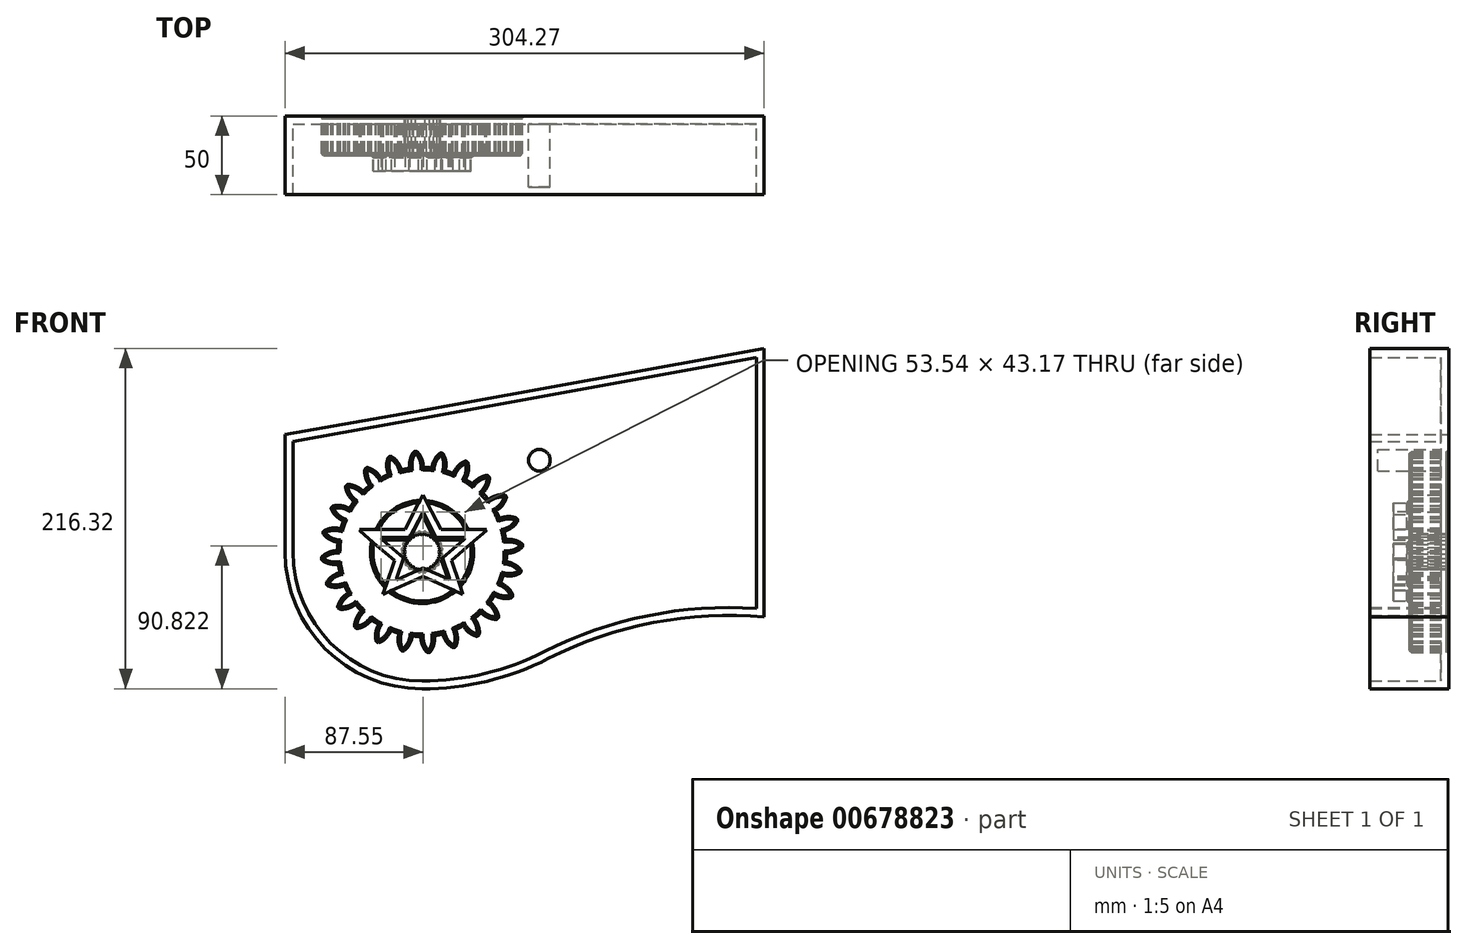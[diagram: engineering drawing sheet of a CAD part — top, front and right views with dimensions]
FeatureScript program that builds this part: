
annotation { "Feature Type Name" : "Feature", "Feature Type Description" : "" }
export const myFeature = defineFeature(function(context is Context, id is Id, definition is map)
    precondition{}
    {
        {
            var Q0;
            Q0=qCreatedBy(makeId("Front.planeOp"),FACE);
            var sketch = newSketch(context, id + "F0", { "sketchPlane" : qUnion([Q0])});
            skCircle(sketch, "E0", {"center": v(0, 0) * mm, "radius": 53.72 * mm});
            skCircle(sketch, "E1", {"center": v(0, 0) * mm, "radius": 58.67 * mm, "construction": true});
            skCircle(sketch, "E2", {"center": v(0, 0) * mm, "radius": 63.5 * mm, "construction": true});
            skLineSegment(sketch, "E3", {"start": v(0, 0) * mm, "end": v(0, 90.28) * mm, "construction": true});
            skLineSegment(sketch, "E4", {"start": v(0, 0) * mm, "end": v(-5.89, 89.83) * mm, "construction": true});
            skLineSegment(sketch, "E5", {"start": v(0, 58.67) * mm, "end": v(-86.47, 27.2) * mm, "construction": true});
            skLineSegment(sketch, "E6", {"start": v(0, 58.67) * mm, "end": v(-89.07, 58.67) * mm, "construction": true});
            skCircle(sketch, "E7", {"center": v(0, 0) * mm, "radius": 55.14 * mm, "construction": true});
            skCircle(sketch, "E8", {"center": v(0, 58.67) * mm, "radius": 14.6 * mm, "construction": true});
            skCircle(sketch, "E9", {"center": v(-13.72, 53.68) * mm, "radius": 14.6 * mm, "construction": true});
            skArc(sketch, "E10", {"start": v(0, 58.67) * mm, "mid": v(-1.18, 61.2) * mm, "end": v(-2.86, 63.44) * mm});
            skArc(sketch, "E11", {"start": v(0.88, 53.71) * mm, "mid": v(0.64, 56.23) * mm, "end": v(0, 58.67) * mm});
            skArc(sketch, "E12.MirrorCS", {"start": v(-7.88, 53.14) * mm, "mid": v(-7.97, 55.66) * mm, "end": v(-7.66, 58.17) * mm});
            skArc(sketch, "E13.MirrorCS", {"start": v(-7.66, 58.17) * mm, "mid": v(-6.82, 60.83) * mm, "end": v(-5.45, 63.27) * mm});
            skArc(sketch, "E14", {"start": v(-2.86, 63.44) * mm, "mid": v(-4.2, 63.93) * mm, "end": v(-5.45, 63.27) * mm});
            skCircle(sketch, "E15", {"center": v(0, 0) * mm, "radius": 31.25 * mm});
            skLineSegment(sketch, "E16", {"start": v(0, 23.83) * mm, "end": v(8.38, 7.72) * mm});
            skLineSegment(sketch, "E17", {"start": v(8.38, 7.72) * mm, "end": v(26.77, 7.72) * mm});
            skLineSegment(sketch, "E18", {"start": v(26.77, 7.72) * mm, "end": v(12.19, -4.72) * mm});
            skLineSegment(sketch, "E19", {"start": v(12.19, -4.72) * mm, "end": v(16.83, -18.55) * mm});
            skLineSegment(sketch, "E20", {"start": v(16.83, -18.55) * mm, "end": v(0, -10.88) * mm});
            skLineSegment(sketch, "E21.MirrorCS", {"start": v(0, 23.83) * mm, "end": v(-8.38, 7.72) * mm});
            skLineSegment(sketch, "E22.MirrorCS", {"start": v(-8.38, 7.72) * mm, "end": v(-26.77, 7.72) * mm});
            skLineSegment(sketch, "E23.MirrorCS", {"start": v(-26.77, 7.72) * mm, "end": v(-12.19, -4.72) * mm});
            skLineSegment(sketch, "E24.MirrorCS", {"start": v(-12.19, -4.72) * mm, "end": v(-16.83, -18.55) * mm});
            skLineSegment(sketch, "E25.MirrorCS", {"start": v(-16.83, -18.55) * mm, "end": v(0, -10.88) * mm});
            skSolve(sketch);
        }
        {
            var Q0;
            {var subQ0=sQuery(id+"F0.wireOp",EDGE,"E0");var subQ1=makeQuery(id+"F0.imprint","INTERSECT",VERTEX,{"derivedFrom":[subQ0,sQuery(id+"F0.wireOp",EDGE,"E12.MirrorCS")]});Q0=makeQuery(id+"F0.imprint","IMPRINT",FACE,{"disambiguationData":[TD([[makeQuery(id+"F0.imprint","IMPRINT",EDGE,{"disambiguationData":[TD([[subQ1,1.0]])],"derivedFrom":subQ0}),1.0]])]});}
            var Q1;
            Q1=makeQuery(id+"F0.imprint","IMPRINT",FACE,{"disambiguationData":[TD([[makeQuery(id+"F0.imprint","IMPRINT",EDGE,{"derivedFrom":sQuery(id+"F0.wireOp",EDGE,"E10")}),1.0]])]});
            var Q2;
            Q2=makeQuery(id+"F0.imprint","IMPRINT",FACE,{"disambiguationData":[TD([[makeQuery(id+"F0.imprint","IMPRINT",EDGE,{"derivedFrom":sQuery(id+"F0.wireOp",EDGE,"E15")}),1.0]])]});
            extrude(context, id + "F1", {"entities" : qUnion([Q0, Q1, Q2]), "depth" : 25 * mm, "offsetDistance" : 25 * mm});
        }
        {
            var Q0;
            Q0=makeQuery(id+"F1.opExtrude","SWEPT_BODY",BODY,{"disambiguationData":[OSD([sQuery(id+"F0.wireOp",EDGE,"E0"),sQuery(id+"F0.wireOp",EDGE,"E10"),sQuery(id+"F0.wireOp",EDGE,"E12.MirrorCS"),sQuery(id+"F0.wireOp",EDGE,"E13.MirrorCS"),sQuery(id+"F0.wireOp",EDGE,"E11"),sQuery(id+"F0.wireOp",EDGE,"E14")])]});
            var Q1;
            Q1=makeQuery(id+"F1.opExtrude","SWEPT_FACE",FACE,{"disambiguationData":[OSD([sQuery(id+"F0.wireOp",EDGE,"E0")])]});
            circularPattern(context, id + "F2", {"entities" : qUnion([Q0]), "axis" : qUnion([Q1]), "angle" : 360 * degree, "instanceCount" : 24, "equalSpace" : true});
        }
        {
            var Q0;
            Q0=makeQuery(id+"F0.imprint","IMPRINT",FACE,{"disambiguationData":[TD([[makeQuery(id+"F0.imprint","IMPRINT",EDGE,{"derivedFrom":sQuery(id+"F0.wireOp",EDGE,"E15")}),1.0]])]});
            extrude(context, id + "F3", {"entities" : qUnion([Q0]), "operationType" : NewBodyOperationType.ADD, "depth" : 35 * mm, "offsetDistance" : 25 * mm});
        }
        {
            var Q0;
            {var subQ0=makeQuery(id+"F1.opExtrude","CAP_FACE",FACE,{"disambiguationData":[OSD([sQuery(id+"F0.wireOp",EDGE,"E0"),sQuery(id+"F0.wireOp",EDGE,"E10"),sQuery(id+"F0.wireOp",EDGE,"E12.MirrorCS"),sQuery(id+"F0.wireOp",EDGE,"E13.MirrorCS"),sQuery(id+"F0.wireOp",EDGE,"E11"),sQuery(id+"F0.wireOp",EDGE,"E14"),sQuery(id+"F0.wireOp",EDGE,"E16"),sQuery(id+"F0.wireOp",EDGE,"E17"),sQuery(id+"F0.wireOp",EDGE,"E18"),sQuery(id+"F0.wireOp",EDGE,"E19"),sQuery(id+"F0.wireOp",EDGE,"E20"),sQuery(id+"F0.wireOp",EDGE,"E21.MirrorCS"),sQuery(id+"F0.wireOp",EDGE,"E22.MirrorCS"),sQuery(id+"F0.wireOp",EDGE,"E23.MirrorCS"),sQuery(id+"F0.wireOp",EDGE,"E24.MirrorCS"),sQuery(id+"F0.wireOp",EDGE,"E25.MirrorCS")])],"isStart":false});Q0=makeQuery(id+"F3.boolean.opBoolean","MERGE",FACE,{"derivedFrom":[subQ0,makeQuery(id+"F2.opPattern","COPY",FACE,{"derivedFrom":subQ0,"instanceName":"1"}),makeQuery(id+"F2.opPattern","COPY",FACE,{"derivedFrom":subQ0,"instanceName":"2"}),makeQuery(id+"F2.opPattern","COPY",FACE,{"derivedFrom":subQ0,"instanceName":"3"}),makeQuery(id+"F2.opPattern","COPY",FACE,{"derivedFrom":subQ0,"instanceName":"4"}),makeQuery(id+"F2.opPattern","COPY",FACE,{"derivedFrom":subQ0,"instanceName":"5"}),makeQuery(id+"F2.opPattern","COPY",FACE,{"derivedFrom":subQ0,"instanceName":"6"}),makeQuery(id+"F2.opPattern","COPY",FACE,{"derivedFrom":subQ0,"instanceName":"7"}),makeQuery(id+"F2.opPattern","COPY",FACE,{"derivedFrom":subQ0,"instanceName":"8"}),makeQuery(id+"F2.opPattern","COPY",FACE,{"derivedFrom":subQ0,"instanceName":"9"}),makeQuery(id+"F2.opPattern","COPY",FACE,{"derivedFrom":subQ0,"instanceName":"10"}),makeQuery(id+"F2.opPattern","COPY",FACE,{"derivedFrom":subQ0,"instanceName":"11"}),makeQuery(id+"F2.opPattern","COPY",FACE,{"derivedFrom":subQ0,"instanceName":"12"}),makeQuery(id+"F2.opPattern","COPY",FACE,{"derivedFrom":subQ0,"instanceName":"13"}),makeQuery(id+"F2.opPattern","COPY",FACE,{"derivedFrom":subQ0,"instanceName":"14"}),makeQuery(id+"F2.opPattern","COPY",FACE,{"derivedFrom":subQ0,"instanceName":"15"}),makeQuery(id+"F2.opPattern","COPY",FACE,{"derivedFrom":subQ0,"instanceName":"16"}),makeQuery(id+"F2.opPattern","COPY",FACE,{"derivedFrom":subQ0,"instanceName":"17"}),makeQuery(id+"F2.opPattern","COPY",FACE,{"derivedFrom":subQ0,"instanceName":"18"}),makeQuery(id+"F2.opPattern","COPY",FACE,{"derivedFrom":subQ0,"instanceName":"19"}),makeQuery(id+"F2.opPattern","COPY",FACE,{"derivedFrom":subQ0,"instanceName":"20"}),makeQuery(id+"F2.opPattern","COPY",FACE,{"derivedFrom":subQ0,"instanceName":"21"}),makeQuery(id+"F2.opPattern","COPY",FACE,{"derivedFrom":subQ0,"instanceName":"22"}),makeQuery(id+"F2.opPattern","COPY",FACE,{"derivedFrom":subQ0,"instanceName":"23"})]});}
            var Q1;
            {var subQ0=sQuery(id+"F0.wireOp",EDGE,"E25.MirrorCS");var subQ1=sQuery(id+"F0.wireOp",EDGE,"E24.MirrorCS");var subQ2=sQuery(id+"F0.wireOp",EDGE,"E23.MirrorCS");var subQ3=sQuery(id+"F0.wireOp",EDGE,"E22.MirrorCS");var subQ4=sQuery(id+"F0.wireOp",EDGE,"E21.MirrorCS");var subQ5=sQuery(id+"F0.wireOp",EDGE,"E20");var subQ6=sQuery(id+"F0.wireOp",EDGE,"E19");var subQ7=sQuery(id+"F0.wireOp",EDGE,"E18");var subQ8=sQuery(id+"F0.wireOp",EDGE,"E17");var subQ9=sQuery(id+"F0.wireOp",EDGE,"E16");var subQ10=makeQuery(id+"F1.opExtrude","CAP_FACE",FACE,{"disambiguationData":[OSD([sQuery(id+"F0.wireOp",EDGE,"E0"),sQuery(id+"F0.wireOp",EDGE,"E10"),sQuery(id+"F0.wireOp",EDGE,"E12.MirrorCS"),sQuery(id+"F0.wireOp",EDGE,"E13.MirrorCS"),sQuery(id+"F0.wireOp",EDGE,"E11"),sQuery(id+"F0.wireOp",EDGE,"E14"),subQ9,subQ8,subQ7,subQ6,subQ5,subQ4,subQ3,subQ2,subQ1,subQ0])],"isStart":true});Q1=makeQuery(id+"F3.boolean.opBoolean","MERGE",FACE,{"derivedFrom":[subQ10,makeQuery(id+"F2.opPattern","COPY",FACE,{"derivedFrom":subQ10,"instanceName":"1"}),makeQuery(id+"F2.opPattern","COPY",FACE,{"derivedFrom":subQ10,"instanceName":"2"}),makeQuery(id+"F2.opPattern","COPY",FACE,{"derivedFrom":subQ10,"instanceName":"3"}),makeQuery(id+"F2.opPattern","COPY",FACE,{"derivedFrom":subQ10,"instanceName":"4"}),makeQuery(id+"F2.opPattern","COPY",FACE,{"derivedFrom":subQ10,"instanceName":"5"}),makeQuery(id+"F2.opPattern","COPY",FACE,{"derivedFrom":subQ10,"instanceName":"6"}),makeQuery(id+"F2.opPattern","COPY",FACE,{"derivedFrom":subQ10,"instanceName":"7"}),makeQuery(id+"F2.opPattern","COPY",FACE,{"derivedFrom":subQ10,"instanceName":"8"}),makeQuery(id+"F2.opPattern","COPY",FACE,{"derivedFrom":subQ10,"instanceName":"9"}),makeQuery(id+"F2.opPattern","COPY",FACE,{"derivedFrom":subQ10,"instanceName":"10"}),makeQuery(id+"F2.opPattern","COPY",FACE,{"derivedFrom":subQ10,"instanceName":"11"}),makeQuery(id+"F2.opPattern","COPY",FACE,{"derivedFrom":subQ10,"instanceName":"12"}),makeQuery(id+"F2.opPattern","COPY",FACE,{"derivedFrom":subQ10,"instanceName":"13"}),makeQuery(id+"F2.opPattern","COPY",FACE,{"derivedFrom":subQ10,"instanceName":"14"}),makeQuery(id+"F2.opPattern","COPY",FACE,{"derivedFrom":subQ10,"instanceName":"15"}),makeQuery(id+"F2.opPattern","COPY",FACE,{"derivedFrom":subQ10,"instanceName":"16"}),makeQuery(id+"F2.opPattern","COPY",FACE,{"derivedFrom":subQ10,"instanceName":"17"}),makeQuery(id+"F2.opPattern","COPY",FACE,{"derivedFrom":subQ10,"instanceName":"18"}),makeQuery(id+"F2.opPattern","COPY",FACE,{"derivedFrom":subQ10,"instanceName":"19"}),makeQuery(id+"F2.opPattern","COPY",FACE,{"derivedFrom":subQ10,"instanceName":"20"}),makeQuery(id+"F2.opPattern","COPY",FACE,{"derivedFrom":subQ10,"instanceName":"21"}),makeQuery(id+"F2.opPattern","COPY",FACE,{"derivedFrom":subQ10,"instanceName":"22"}),makeQuery(id+"F2.opPattern","COPY",FACE,{"derivedFrom":subQ10,"instanceName":"23"}),makeQuery(id+"F3.opExtrude","CAP_FACE",FACE,{"disambiguationData":[OSD([sQuery(id+"F0.wireOp",EDGE,"E15"),subQ9,subQ8,subQ7,subQ6,subQ5,subQ4,subQ3,subQ2,subQ1,subQ0])],"isStart":true})]});}
            chamfer(context, id + "F4", {"entities" : qUnion([Q0, Q1]), "width" : 1.5 * mm, "tangentPropagation" : true});
        }
        {
            var Q0;
            Q0=qCreatedBy(makeId("Front.planeOp"),FACE);
            var sketch = newSketch(context, id + "F5", { "sketchPlane" : qUnion([Q0])});
            skArc(sketch, "E26", {"start": v(-86.95, 0) * mm, "mid": v(-61.49, -61.49) * mm, "end": v(0, -86.95) * mm});
            skLineSegment(sketch, "E27", {"start": v(-86.95, 0) * mm, "end": v(-86.95, 74.5) * mm});
            skArc(sketch, "E28", {"start": v(0, -86.95) * mm, "mid": v(41.21, -82.09) * mm, "end": v(80.16, -67.75) * mm});
            skLineSegment(sketch, "E29", {"start": v(-86.95, 74.5) * mm, "end": v(0, 89.97) * mm});
            skLineSegment(sketch, "E30", {"start": v(0, 89.97) * mm, "end": v(217.32, 129.37) * mm});
            skLineSegment(sketch, "E31", {"start": v(217.32, 129.37) * mm, "end": v(217.32, -41.28) * mm});
            skArc(sketch, "E32", {"start": v(217.32, -41.28) * mm, "mid": v(146.88, -44.87) * mm, "end": v(80.16, -67.75) * mm});
            skLineSegment(sketch, "E33", {"start": v(0.6, 25.45) * mm, "end": v(8.98, 9.35) * mm});
            skLineSegment(sketch, "E34", {"start": v(8.98, 9.35) * mm, "end": v(27.37, 9.35) * mm});
            skLineSegment(sketch, "E35", {"start": v(27.37, 9.35) * mm, "end": v(12.79, -3.1) * mm});
            skLineSegment(sketch, "E36", {"start": v(12.79, -3.1) * mm, "end": v(17.43, -16.92) * mm});
            skLineSegment(sketch, "E37", {"start": v(17.43, -16.92) * mm, "end": v(0.6, -9.26) * mm});
            skLineSegment(sketch, "E38.MirrorCS", {"start": v(0.6, 25.45) * mm, "end": v(-7.78, 9.35) * mm});
            skLineSegment(sketch, "E39.MirrorCS", {"start": v(-7.78, 9.35) * mm, "end": v(-26.17, 9.35) * mm});
            skLineSegment(sketch, "E40.MirrorCS", {"start": v(-26.17, 9.35) * mm, "end": v(-11.59, -3.1) * mm});
            skLineSegment(sketch, "E41.MirrorCS", {"start": v(-11.59, -3.1) * mm, "end": v(-16.24, -16.92) * mm});
            skLineSegment(sketch, "E42.MirrorCS", {"start": v(-16.24, -16.92) * mm, "end": v(0.6, -9.26) * mm});
            skLineSegment(sketch, "E43", {"start": v(0.6, 24.67) * mm, "end": v(8.98, 8.56) * mm});
            skLineSegment(sketch, "E44", {"start": v(8.98, 8.56) * mm, "end": v(27.37, 8.56) * mm});
            skLineSegment(sketch, "E45", {"start": v(27.37, 8.56) * mm, "end": v(12.79, -3.88) * mm});
            skLineSegment(sketch, "E46", {"start": v(12.79, -3.88) * mm, "end": v(17.43, -17.71) * mm});
            skLineSegment(sketch, "E47", {"start": v(17.43, -17.71) * mm, "end": v(0.6, -10.04) * mm});
            skLineSegment(sketch, "E48.MirrorCS", {"start": v(0.6, 24.67) * mm, "end": v(-7.78, 8.56) * mm});
            skLineSegment(sketch, "E49.MirrorCS", {"start": v(-7.78, 8.56) * mm, "end": v(-26.17, 8.56) * mm});
            skLineSegment(sketch, "E50.MirrorCS", {"start": v(-26.17, 8.56) * mm, "end": v(-11.59, -3.88) * mm});
            skLineSegment(sketch, "E51.MirrorCS", {"start": v(-11.59, -3.88) * mm, "end": v(-16.24, -17.71) * mm});
            skLineSegment(sketch, "E52.MirrorCS", {"start": v(-16.24, -17.71) * mm, "end": v(0.6, -10.04) * mm});
            skSolve(sketch);
        }
        {
            var Q0;
            Q0=makeQuery(id+"F5.imprint","IMPRINT",FACE,{"disambiguationData":[TD([[makeQuery(id+"F5.imprint","IMPRINT",EDGE,{"derivedFrom":sQuery(id+"F5.wireOp",EDGE,"E26")}),1.0]])]});
            extrude(context, id + "F6", {"entities" : qUnion([Q0]), "depth" : 50 * mm, "offsetDistance" : 25 * mm});
        }
        {
            var Q0;
            Q0=makeQuery(id+"F6.opExtrude","CAP_FACE",FACE,{"disambiguationData":[OSD([sQuery(id+"F5.wireOp",EDGE,"E26"),sQuery(id+"F5.wireOp",EDGE,"E27"),sQuery(id+"F5.wireOp",EDGE,"E28"),sQuery(id+"F5.wireOp",EDGE,"E29"),sQuery(id+"F5.wireOp",EDGE,"E30"),sQuery(id+"F5.wireOp",EDGE,"E31"),sQuery(id+"F5.wireOp",EDGE,"E32")])],"isStart":false});
            shell(context, id + "F7", {"entities" : qUnion([Q0]), "thickness" : 5 * mm});
        }
        {
            var Q0;
            {var subQ0=sQuery(id+"F5.wireOp",EDGE,"E52.MirrorCS");var subQ1=sQuery(id+"F5.wireOp",EDGE,"E51.MirrorCS");var subQ2=sQuery(id+"F5.wireOp",EDGE,"E50.MirrorCS");var subQ3=sQuery(id+"F5.wireOp",EDGE,"E49.MirrorCS");var subQ4=sQuery(id+"F5.wireOp",EDGE,"E47");var subQ5=sQuery(id+"F5.wireOp",EDGE,"E46");var subQ6=sQuery(id+"F5.wireOp",EDGE,"E45");var subQ7=sQuery(id+"F5.wireOp",EDGE,"E44");var subQ8=sQuery(id+"F5.wireOp",EDGE,"E42.MirrorCS");var subQ9=sQuery(id+"F5.wireOp",EDGE,"E41.MirrorCS");var subQ10=sQuery(id+"F5.wireOp",EDGE,"E40.MirrorCS");var subQ11=sQuery(id+"F5.wireOp",EDGE,"E39.MirrorCS");var subQ12=sQuery(id+"F5.wireOp",EDGE,"E38.MirrorCS");var subQ13=sQuery(id+"F5.wireOp",EDGE,"E37");var subQ14=sQuery(id+"F5.wireOp",EDGE,"E36");var subQ15=sQuery(id+"F5.wireOp",EDGE,"E35");var subQ16=sQuery(id+"F5.wireOp",EDGE,"E34");var subQ17=sQuery(id+"F5.wireOp",EDGE,"E33");var subQ18=sQuery(id+"F5.wireOp",EDGE,"E32");var subQ19=sQuery(id+"F5.wireOp",EDGE,"E31");var subQ20=sQuery(id+"F5.wireOp",EDGE,"E30");var subQ21=sQuery(id+"F5.wireOp",EDGE,"E29");var subQ22=sQuery(id+"F5.wireOp",EDGE,"E28");var subQ23=sQuery(id+"F5.wireOp",EDGE,"E27");var subQ24=sQuery(id+"F5.wireOp",EDGE,"E26");Q0=makeQuery(id+"F7.opShell","OFFSET_FACE",FACE,{"disambiguationData":[OSD([subQ24,subQ23,subQ22,subQ21,subQ20,subQ19,subQ18,subQ17,subQ16,subQ15,subQ14,subQ13,subQ12,subQ11,subQ10,subQ9,subQ8,subQ7,subQ6,subQ5,subQ4,subQ3,subQ2,subQ1,subQ0]),TDD([makeQuery(id+"F6.opExtrude","CAP_FACE",FACE,{"disambiguationData":[OSD([subQ24,subQ23,subQ22,subQ21,subQ20,subQ19,subQ18,subQ17,subQ16,subQ15,subQ14,subQ13,subQ12,subQ11,subQ10,subQ9,subQ8,subQ7,subQ6,subQ5,subQ4,subQ3,subQ2,subQ1,subQ0])],"isStart":false})])]});}
            extrude(context, id + "F8", {"entities" : qUnion([Q0]), "operationType" : NewBodyOperationType.REMOVE, "oppositeDirection" : true, "depth" : 25 * mm, "offsetDistance" : 25 * mm});
        }
        {
            var Q0;
            {var subQ0=sQuery(id+"F5.wireOp",EDGE,"E52.MirrorCS");var subQ1=sQuery(id+"F5.wireOp",EDGE,"E51.MirrorCS");var subQ2=sQuery(id+"F5.wireOp",EDGE,"E50.MirrorCS");var subQ3=sQuery(id+"F5.wireOp",EDGE,"E49.MirrorCS");var subQ4=sQuery(id+"F5.wireOp",EDGE,"E47");var subQ5=sQuery(id+"F5.wireOp",EDGE,"E46");var subQ6=sQuery(id+"F5.wireOp",EDGE,"E45");var subQ7=sQuery(id+"F5.wireOp",EDGE,"E44");var subQ8=sQuery(id+"F5.wireOp",EDGE,"E42.MirrorCS");var subQ9=sQuery(id+"F5.wireOp",EDGE,"E41.MirrorCS");var subQ10=sQuery(id+"F5.wireOp",EDGE,"E40.MirrorCS");var subQ11=sQuery(id+"F5.wireOp",EDGE,"E39.MirrorCS");var subQ12=sQuery(id+"F5.wireOp",EDGE,"E38.MirrorCS");var subQ13=sQuery(id+"F5.wireOp",EDGE,"E37");var subQ14=sQuery(id+"F5.wireOp",EDGE,"E36");var subQ15=sQuery(id+"F5.wireOp",EDGE,"E35");var subQ16=sQuery(id+"F5.wireOp",EDGE,"E34");var subQ17=sQuery(id+"F5.wireOp",EDGE,"E33");var subQ18=sQuery(id+"F5.wireOp",EDGE,"E32");var subQ19=sQuery(id+"F5.wireOp",EDGE,"E31");var subQ20=sQuery(id+"F5.wireOp",EDGE,"E30");var subQ21=sQuery(id+"F5.wireOp",EDGE,"E29");var subQ22=sQuery(id+"F5.wireOp",EDGE,"E28");var subQ23=sQuery(id+"F5.wireOp",EDGE,"E27");var subQ24=sQuery(id+"F5.wireOp",EDGE,"E26");Q0=makeQuery(id+"F7.opShell","OFFSET_FACE",FACE,{"disambiguationData":[OSD([subQ24,subQ23,subQ22,subQ21,subQ20,subQ19,subQ18,subQ17,subQ16,subQ15,subQ14,subQ13,subQ12,subQ11,subQ10,subQ9,subQ8,subQ7,subQ6,subQ5,subQ4,subQ3,subQ2,subQ1,subQ0]),TDD([makeQuery(id+"F6.opExtrude","CAP_FACE",FACE,{"disambiguationData":[OSD([subQ24,subQ23,subQ22,subQ21,subQ20,subQ19,subQ18,subQ17,subQ16,subQ15,subQ14,subQ13,subQ12,subQ11,subQ10,subQ9,subQ8,subQ7,subQ6,subQ5,subQ4,subQ3,subQ2,subQ1,subQ0])],"isStart":true})])]});}
            var sketch = newSketch(context, id + "F9", { "sketchPlane" : qUnion([Q0])});
            skCircle(sketch, "E53", {"center": v(74.54, 58.25) * mm, "radius": 6.88 * mm});
            skSolve(sketch);
        }
        {
            var Q0;
            Q0=makeQuery(id+"F9.imprint","IMPRINT",FACE,{"disambiguationData":[TD([[makeQuery(id+"F9.imprint","IMPRINT",EDGE,{"derivedFrom":sQuery(id+"F9.wireOp",EDGE,"E53")}),1.0]])]});
            extrude(context, id + "F10", {"entities" : qUnion([Q0]), "operationType" : NewBodyOperationType.ADD, "depth" : 40 * mm, "offsetDistance" : 25 * mm});
        }
    });
